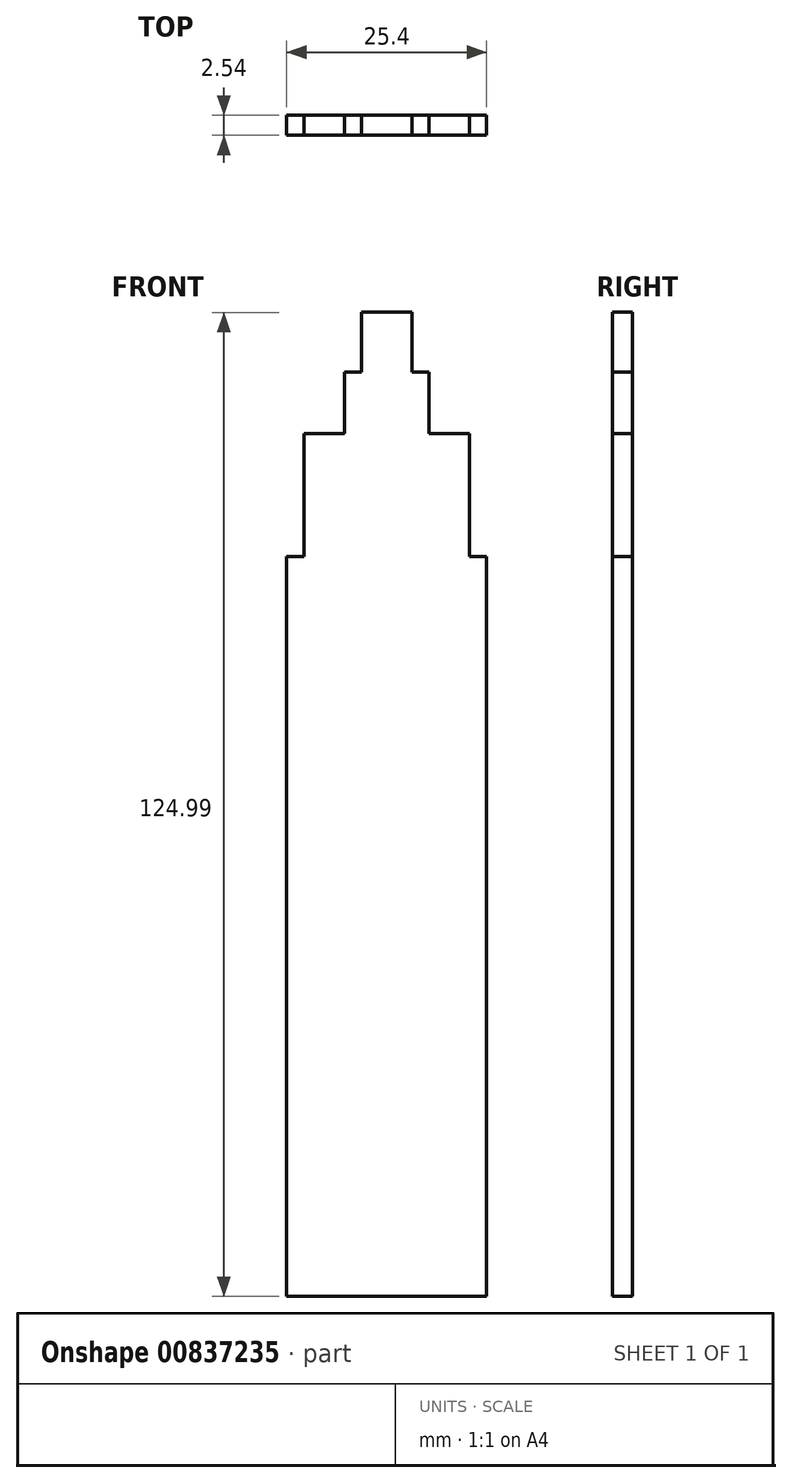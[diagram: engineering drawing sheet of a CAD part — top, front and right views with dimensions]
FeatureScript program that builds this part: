
annotation { "Feature Type Name" : "Feature", "Feature Type Description" : "" }
export const myFeature = defineFeature(function(context is Context, id is Id, definition is map)
    precondition{}
    {
        {
            var Q0;
            Q0=qCreatedBy(makeId("Front.planeOp"),FACE);
            var sketch = newSketch(context, id + "F0", { "sketchPlane" : qUnion([Q0])});
            skLineSegment(sketch, "E0", {"start": v(0, 0) * mm, "end": v(-12.7, 0) * mm});
            skLineSegment(sketch, "E1.MirrorCS", {"start": v(0, 0) * mm, "end": v(12.7, 0) * mm});
            skLineSegment(sketch, "E2", {"start": v(-12.7, 0) * mm, "end": v(-12.7, 93.98) * mm});
            skLineSegment(sketch, "E3", {"start": v(-3.2, 125) * mm, "end": v(3.2, 125) * mm});
            skLineSegment(sketch, "E4", {"start": v(12.7, 93.98) * mm, "end": v(12.7, 0) * mm});
            skLineSegment(sketch, "E5", {"start": v(-12.7, 93.98) * mm, "end": v(12.7, 93.98) * mm});
            skLineSegment(sketch, "E6", {"start": v(-10.48, 109.62) * mm, "end": v(10.48, 109.62) * mm});
            skLineSegment(sketch, "E7", {"start": v(-5.36, 117.4) * mm, "end": v(5.36, 117.4) * mm});
            skLineSegment(sketch, "E8", {"start": v(-10.48, 93.98) * mm, "end": v(-10.48, 109.62) * mm});
            skLineSegment(sketch, "E9", {"start": v(10.48, 93.98) * mm, "end": v(10.48, 109.62) * mm});
            skLineSegment(sketch, "E10", {"start": v(-5.36, 109.62) * mm, "end": v(-5.36, 117.4) * mm});
            skLineSegment(sketch, "E11", {"start": v(5.36, 109.62) * mm, "end": v(5.36, 117.4) * mm});
            skLineSegment(sketch, "E12", {"start": v(-3.2, 117.4) * mm, "end": v(-3.2, 125) * mm});
            skLineSegment(sketch, "E13", {"start": v(3.2, 117.4) * mm, "end": v(3.2, 125) * mm});
            skSolve(sketch);
        }
        {
            var Q0;
            Q0=makeQuery(id+"F0.imprint","IMPRINT",FACE,{"disambiguationData":[TD([[makeQuery(id+"F0.imprint","IMPRINT",EDGE,{"derivedFrom":sQuery(id+"F0.wireOp",EDGE,"E0")}),-1.0]])]});
            var Q1;
            {var subQ4=sQuery(id+"F0.wireOp",EDGE,"E8");Q1=makeQuery(id+"F0.imprint","IMPRINT",FACE,{"disambiguationData":[TD([[makeQuery(id+"F0.imprint","IMPRINT",EDGE,{"derivedFrom":subQ4}),-1.0]])]});}
            var Q2;
            {var subQ4=sQuery(id+"F0.wireOp",EDGE,"E10");Q2=makeQuery(id+"F0.imprint","IMPRINT",FACE,{"disambiguationData":[TD([[makeQuery(id+"F0.imprint","IMPRINT",EDGE,{"derivedFrom":subQ4}),-1.0]])]});}
            var Q3;
            Q3=makeQuery(id+"F0.imprint","IMPRINT",FACE,{"disambiguationData":[TD([[makeQuery(id+"F0.imprint","IMPRINT",EDGE,{"derivedFrom":sQuery(id+"F0.wireOp",EDGE,"E3")}),-1.0]])]});
            extrude(context, id + "F1", {"entities" : qUnion([Q0, Q1, Q2, Q3]), "oppositeDirection" : true, "depth" : 2.54 * mm, "offsetDistance" : 25.4 * mm});
        }
    });
